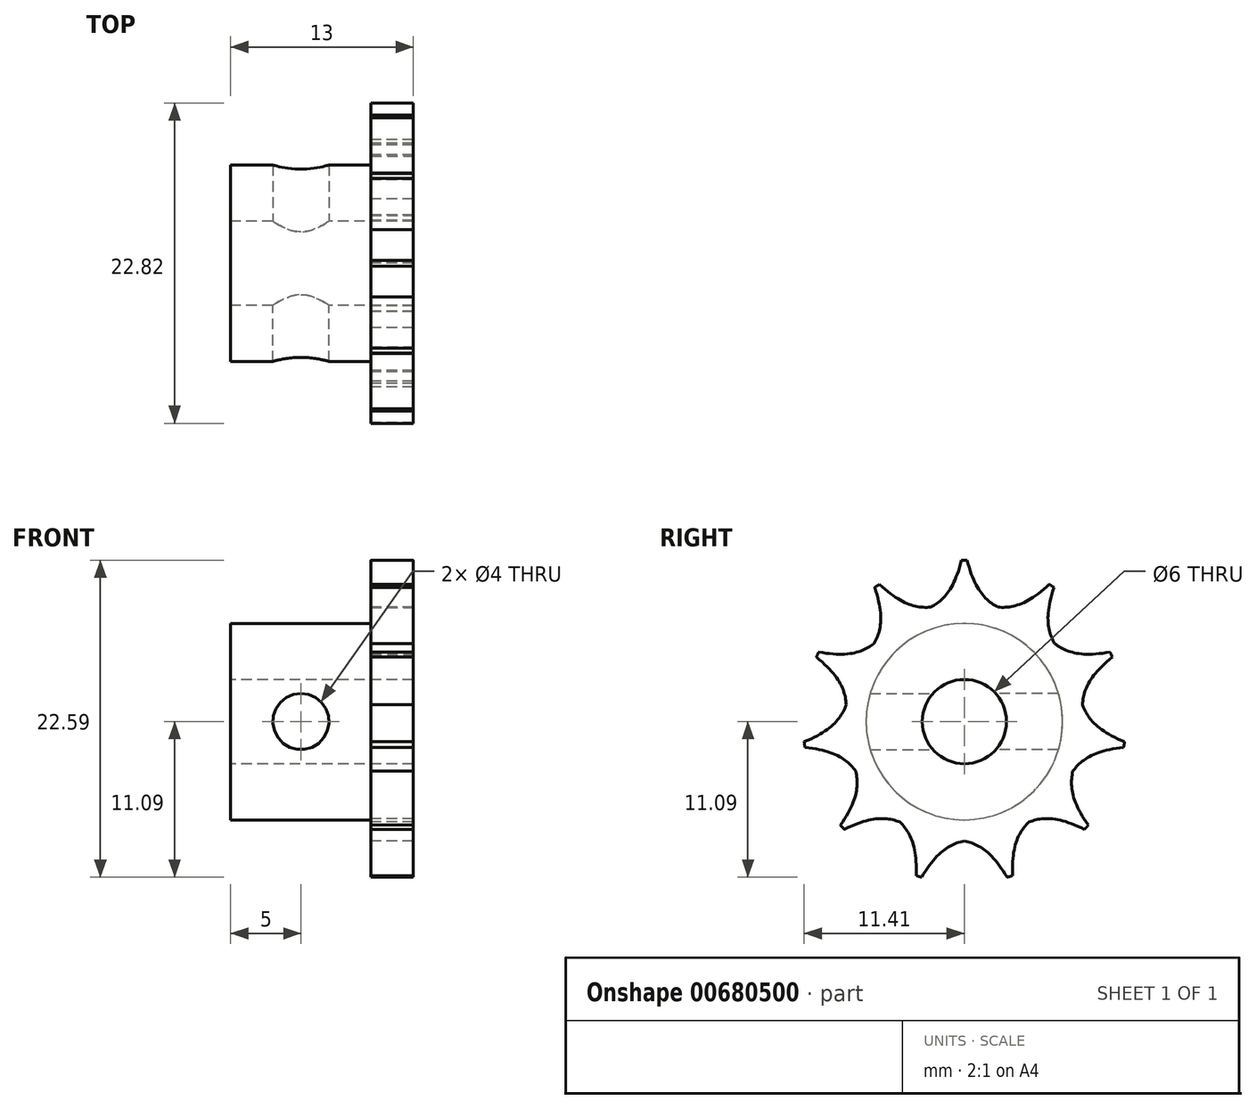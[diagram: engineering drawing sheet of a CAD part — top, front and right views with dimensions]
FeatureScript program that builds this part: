
annotation { "Feature Type Name" : "Feature", "Feature Type Description" : "" }
export const myFeature = defineFeature(function(context is Context, id is Id, definition is map)
    precondition{}
    {
        {
            var Q0;
            Q0=qCreatedBy(makeId("Right.planeOp"),FACE);
            var sketch = newSketch(context, id + "F0", { "sketchPlane" : qUnion([Q0])});
            skArc(sketch, "E0", {"start": v(0.2, 11.5) * mm, "mid": v(0, 11.5) * mm, "end": v(-0.2, 11.5) * mm});
            skPoint(sketch, "E1.orphan", {"position": v(2.8, 9.5) * mm});
            skLineSegment(sketch, "E2", {"start": v(0, 0) * mm, "end": v(-2.4, 8.16) * mm});
            skPoint(sketch, "E3.orphan", {"position": v(-1.77, 8.31) * mm});
            skPoint(sketch, "E4.orphan", {"position": v(1.77, 8.31) * mm});
            skLineSegment(sketch, "E5.MirrorCS", {"start": v(0, 0) * mm, "end": v(2.4, 8.16) * mm});
            skPoint(sketch, "E6.orphan", {"position": v(0.2, 11.5) * mm});
            skPoint(sketch, "E7.MirrorCS.end.orphan", {"position": v(1.92, 9.02) * mm});
            skFitSpline(sketch, "E8", {"points": [v(-2.4, 8.16) * mm, v(-0.2, 11.5) * mm], "startDerivative": vector(2.72, 1.49) * mm, "endDerivative": vector(1.6, 6.27) * mm});
            skFitSpline(sketch, "E9.MirrorCS", {"points": [v(2.4, 8.16) * mm, v(0.2, 11.5) * mm], "startDerivative": vector(-2.72, 1.49) * mm, "endDerivative": vector(-1.6, 6.27) * mm});
            skPoint(sketch, "E10.orphan", {"position": v(2.06, 9.7) * mm});
            skPoint(sketch, "E11.trimOffspring.start.orphan", {"position": v(-2.06, 9.7) * mm});
            skPoint(sketch, "E12.orphan", {"position": v(-2.8, 9.5) * mm});
            skSolve(sketch);
        }
        {
            var Q0;
            Q0 = qSketchRegion(id + "F0", true);
            extrude(context, id + "F1", {"entities" : qUnion([Q0]), "depth" : 3 * mm, "offsetDistance" : 25 * mm});
        }
        {
            var Q0;
            Q0=makeQuery(id+"F1.opExtrude","SWEPT_BODY",BODY,{"disambiguationData":[OSD([sQuery(id+"F0.wireOp",EDGE,"E0"),sQuery(id+"F0.wireOp",EDGE,"E2"),sQuery(id+"F0.wireOp",EDGE,"E5.MirrorCS"),sQuery(id+"F0.wireOp",EDGE,"E8"),sQuery(id+"F0.wireOp",EDGE,"E9.MirrorCS")])]});
            var Q1;
            Q1=makeQuery(id+"F1.opExtrude","SWEPT_EDGE",EDGE,{"disambiguationData":[OSD([sQuery(id+"F0.wireOp",EDGE,"E2"),sQuery(id+"F0.wireOp",EDGE,"E5.MirrorCS")])]});
            circularPattern(context, id + "F2", {"operationType" : NewBodyOperationType.ADD, "entities" : qUnion([Q0]), "axis" : qUnion([Q1]), "angle" : 360 * degree, "instanceCount" : 11, "equalSpace" : true});
        }
        {
            var Q0;
            {var subQ0=makeQuery(id+"F1.opExtrude","CAP_FACE",FACE,{"disambiguationData":[OSD([sQuery(id+"F0.wireOp",EDGE,"E0"),sQuery(id+"F0.wireOp",EDGE,"E2"),sQuery(id+"F0.wireOp",EDGE,"E5.MirrorCS"),sQuery(id+"F0.wireOp",EDGE,"E8"),sQuery(id+"F0.wireOp",EDGE,"E9.MirrorCS")])],"isStart":true});Q0=makeQuery(id+"F2.boolean.opBoolean","MERGE",FACE,{"derivedFrom":[subQ0,makeQuery(id+"F2.opPattern","COPY",FACE,{"derivedFrom":subQ0,"instanceName":"1"}),makeQuery(id+"F2.opPattern","COPY",FACE,{"derivedFrom":subQ0,"instanceName":"2"}),makeQuery(id+"F2.opPattern","COPY",FACE,{"derivedFrom":subQ0,"instanceName":"3"}),makeQuery(id+"F2.opPattern","COPY",FACE,{"derivedFrom":subQ0,"instanceName":"4"}),makeQuery(id+"F2.opPattern","COPY",FACE,{"derivedFrom":subQ0,"instanceName":"5"}),makeQuery(id+"F2.opPattern","COPY",FACE,{"derivedFrom":subQ0,"instanceName":"6"}),makeQuery(id+"F2.opPattern","COPY",FACE,{"derivedFrom":subQ0,"instanceName":"7"}),makeQuery(id+"F2.opPattern","COPY",FACE,{"derivedFrom":subQ0,"instanceName":"8"}),makeQuery(id+"F2.opPattern","COPY",FACE,{"derivedFrom":subQ0,"instanceName":"9"}),makeQuery(id+"F2.opPattern","COPY",FACE,{"derivedFrom":subQ0,"instanceName":"10"})]});}
            var sketch = newSketch(context, id + "F3", { "sketchPlane" : qUnion([Q0])});
            skCircle(sketch, "E13", {"center": v(0, 0) * mm, "radius": 7 * mm});
            skSolve(sketch);
        }
        {
            var Q0;
            Q0 = qSketchRegion(id + "F3", true);
            extrude(context, id + "F4", {"entities" : qUnion([Q0]), "operationType" : NewBodyOperationType.ADD, "depth" : 10 * mm, "offsetDistance" : 25 * mm});
        }
        {
            var Q0;
            Q0=makeQuery(id+"F4.opExtrude","CAP_FACE",FACE,{"disambiguationData":[OSD([sQuery(id+"F3.wireOp",EDGE,"E13")])],"isStart":false});
            var sketch = newSketch(context, id + "F5", { "sketchPlane" : qUnion([Q0])});
            skCircle(sketch, "E14", {"center": v(0, 0) * mm, "radius": 3 * mm});
            skSolve(sketch);
        }
        {
            var Q0;
            Q0 = qSketchRegion(id + "F5", true);
            extrude(context, id + "F6", {"entities" : qUnion([Q0]), "operationType" : NewBodyOperationType.REMOVE, "endBound" : BoundingType.THROUGH_ALL, "oppositeDirection" : true, "depth" : 25 * mm, "offsetDistance" : 25 * mm});
        }
        {
            var Q0;
            Q0=qCreatedBy(makeId("Front.planeOp"),FACE);
            var sketch = newSketch(context, id + "F7", { "sketchPlane" : qUnion([Q0])});
            skCircle(sketch, "E15", {"center": v(-5, 0) * mm, "radius": 2 * mm});
            skSolve(sketch);
        }
        {
            var Q0;
            Q0 = qSketchRegion(id + "F7", true);
            extrude(context, id + "F8", {"entities" : qUnion([Q0]), "operationType" : NewBodyOperationType.REMOVE, "endBound" : BoundingType.THROUGH_ALL, "oppositeDirection" : true, "depth" : 25 * mm, "offsetDistance" : 25 * mm});
        }
        {
            var Q0;
            Q0=qCreatedBy(makeId("Front.planeOp"),FACE);
            var sketch = newSketch(context, id + "F9", { "sketchPlane" : qUnion([Q0])});
            skCircle(sketch, "E16", {"center": v(-5, 0) * mm, "radius": 2 * mm});
            skSolve(sketch);
        }
        {
            var Q0;
            Q0 = qSketchRegion(id + "F9", true);
            extrude(context, id + "F10", {"entities" : qUnion([Q0]), "operationType" : NewBodyOperationType.REMOVE, "endBound" : BoundingType.THROUGH_ALL, "depth" : 25 * mm, "offsetDistance" : 25 * mm});
        }
    });
